# Revit family: VLPGFP1501-xxxWS8xxBxxxx
name_source: partatom
category: Oprawy oświetleniowe
revit_build: Autodesk Revit 2017 (Build: 20190507_1515(x64)
units: mm (PartAtom-declared; Revit-internal decimal feet)

## family parameters
Numer OmniClass = 23.80.70.11
Obiekt nadrzędny = Powierzchnia
Punkt obliczania pomieszczeń = Nie
Tnij formami wycięć po wczytaniu = Nie
Typ części = Normalny
Tytuł OmniClass = Luminaries for Internal Lighting
Współdzielony = Nie
Wymiar okrągłego złącza = Użyj średnicy
Źródło światła = Tak

## types (6) — shared parameters
Emituj kształt widoczny w renderingu = Nie
Emituj z długości prostokąta = 30 mm  [stored 0.0984252 ft]
Emituj z szerokości prostokąta = 1469 mm  [stored 4.81955 ft]
Filtr koloru = 16777215
Kod zespołu = D5020200
Lampa = LED
Odchylenie kierunku = 90.00°
Plik sieci fotometrycznej = VLPGFP1501-7DAWS840B0750.IES
Producent = RIDI Leuchten GmbH
URL = www.ridi.de
Zmiana temperatury barwowej przyciemniania lampy = <Brak>
brand = RIDI
conformity mark = CE
electrical safety class = 1
height = 66 mm  [stored 0.216535 ft]
ingress protection (IP) code = IP54
length = 1500 mm  [stored 4.92126 ft]
nominal frequency = 50-60Hz
nominal voltage = 230
voltage type (AC, DC, UC) = AC
width = 67 mm
zero-valued in all types: Domyślna rzędna

## per-type parameters (varying)
| type | Model | Obciążenie pozorne | rated input power | weight |
| VLPGFP1501-7DAWS840B0750 | 1561208 | 48 VA | 48 | 1.91 kg |
| VLPGFP1501-5NDWS840B0900-RF | 1551286 | 55 VA | 55 | 2,18 kg |
| VLPGFP1501-7DAWS850B0750 | 1561231 | 48 VA | 48 | 1.91 kg |
| VLPGFP1501-5NDWS850B0900-RF | 1551288 | 55 VA | 55 | 2.18 kg |
| VLPGFP1501-7DAWS865B0750 | 1561223 | 48 VA | 48 | 1.91 kg |
| VLPGFP1501-5NDWS865B0900-RF | 1551290 | 55 VA | 55 | 2.18 kg |

note: column(s) folded — value = type name in every type: product name

note: [stored X ft] marks values corroborated as IEEE doubles in the binary element streams (Revit-internal decimal feet)
